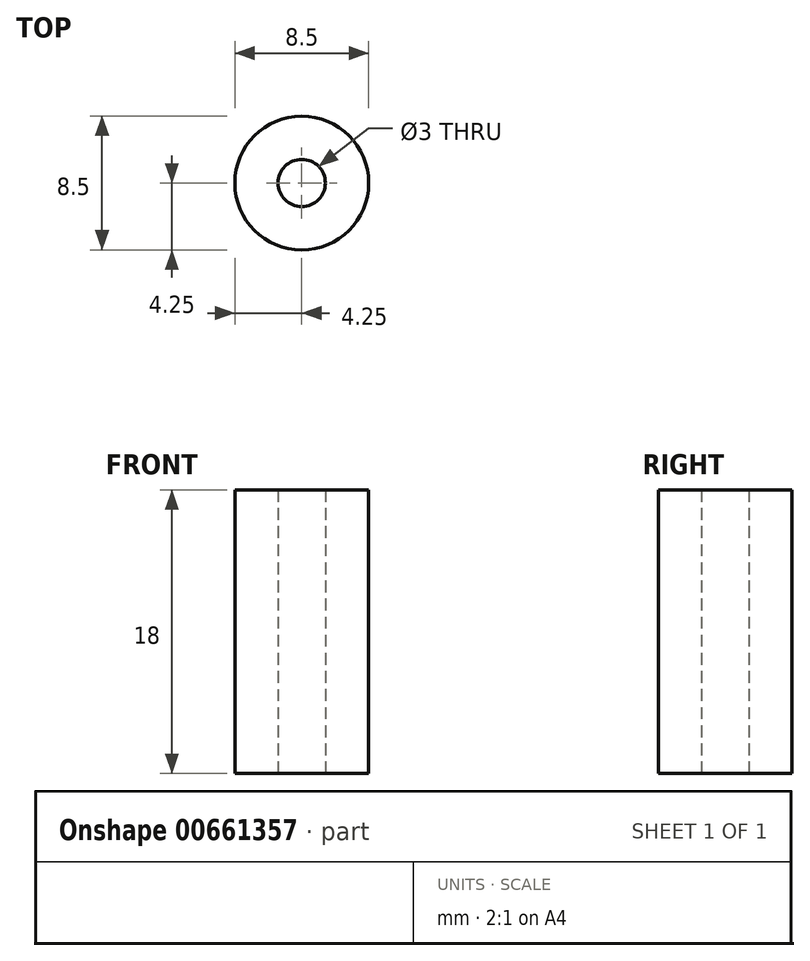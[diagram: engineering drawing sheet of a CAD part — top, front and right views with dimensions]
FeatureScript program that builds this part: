
annotation { "Feature Type Name" : "Feature", "Feature Type Description" : "" }
export const myFeature = defineFeature(function(context is Context, id is Id, definition is map)
    precondition{}
    {
        {
            var Q0;
            Q0=qCreatedBy(makeId("Front.planeOp"),FACE);
            var sketch = newSketch(context, id + "F0", { "sketchPlane" : qUnion([Q0])});
            skLineSegment(sketch, "E0", {"start": v(0, 0) * mm, "end": v(-1.5, 0) * mm, "construction": true});
            skLineSegment(sketch, "E1", {"start": v(-1.5, 0) * mm, "end": v(-4.25, 0) * mm});
            skLineSegment(sketch, "E2", {"start": v(-4.25, 0) * mm, "end": v(-4.25, 18) * mm});
            skLineSegment(sketch, "E3", {"start": v(-4.25, 18) * mm, "end": v(-1.5, 18) * mm});
            skLineSegment(sketch, "E4", {"start": v(-1.5, 18) * mm, "end": v(-1.5, 0) * mm});
            skLineSegment(sketch, "E5", {"start": v(0, 0) * mm, "end": v(0, 18) * mm, "construction": true});
            skSolve(sketch);
        }
        {
            var Q0;
            Q0=qSketchRegion(id+"F0",true);
            var Q1;
            Q1=sQuery(id+"F0.wireOp",EDGE,"E5");
            revolve(context, id + "F1", {"entities" : qUnion([Q0]), "axis" : qUnion([Q1]), "revolveType" : RevolveType.FULL});
        }
    });
